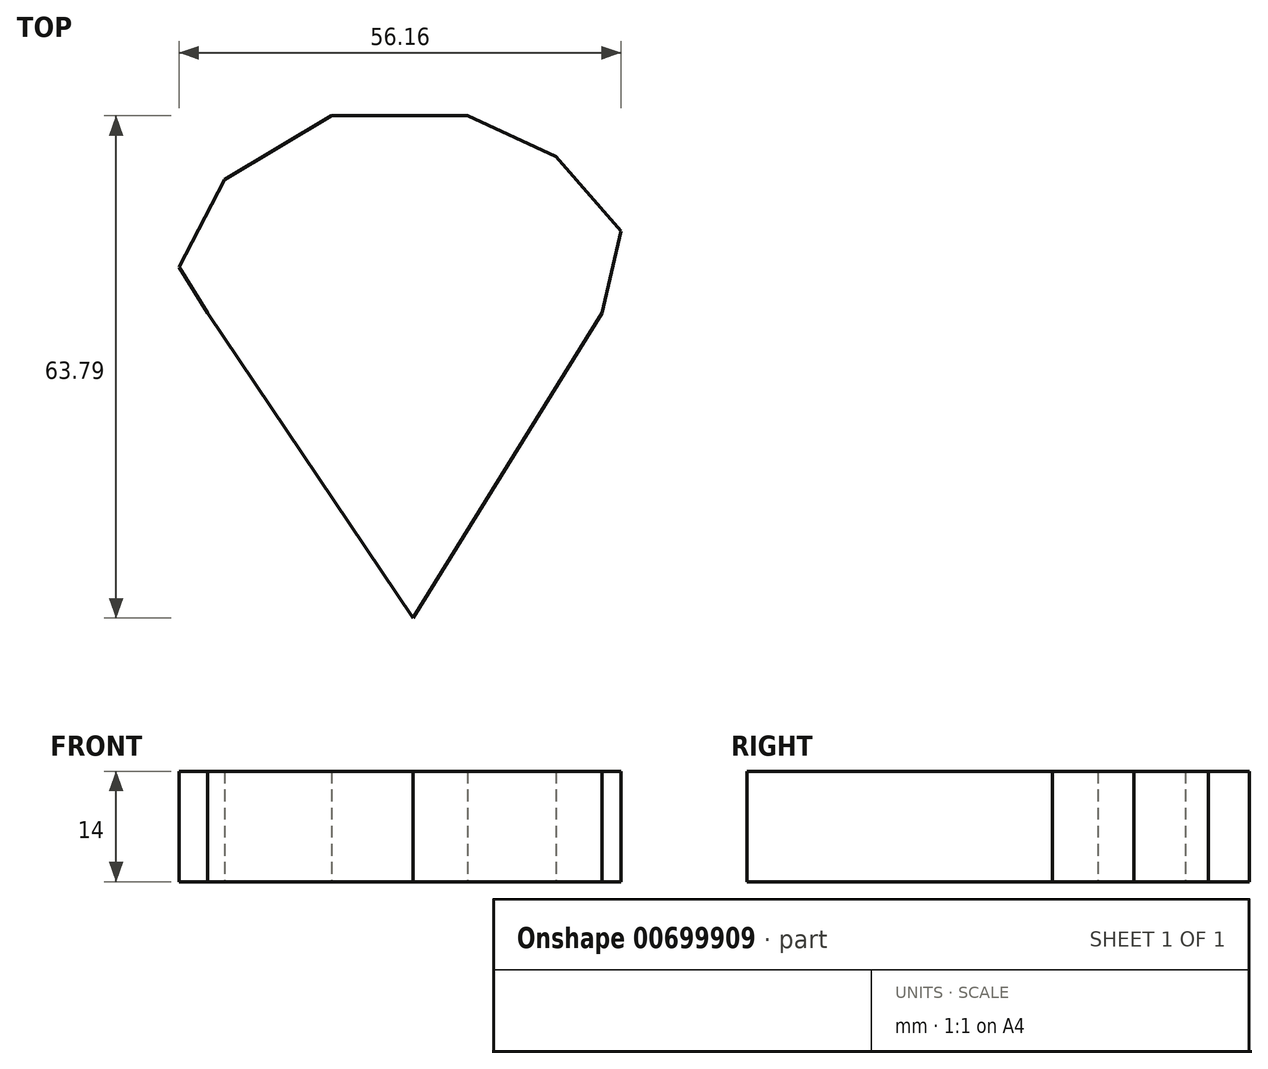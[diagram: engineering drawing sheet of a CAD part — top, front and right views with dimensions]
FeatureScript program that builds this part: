
annotation { "Feature Type Name" : "Feature", "Feature Type Description" : "" }
export const myFeature = defineFeature(function(context is Context, id is Id, definition is map)
    precondition{}
    {
        {
            var Q0;
            Q0=qCreatedBy(makeId("Top.planeOp"),FACE);
            var sketch = newSketch(context, id + "F0", { "sketchPlane" : qUnion([Q0])});
            skLineSegment(sketch, "E0.bottom", {"start": v(-39.53, 38.3) * mm, "end": v(60.28, 38.3) * mm});
            skLineSegment(sketch, "E0.top", {"start": v(-39.53, -55.7) * mm, "end": v(60.28, -55.7) * mm});
            skLineSegment(sketch, "E0.left", {"start": v(-39.53, 38.3) * mm, "end": v(-39.53, -55.7) * mm});
            skLineSegment(sketch, "E0.right", {"start": v(60.28, 38.3) * mm, "end": v(60.28, -55.7) * mm});
            skLineSegment(sketch, "E1", {"start": v(10.38, -55.7) * mm, "end": v(-15.72, -16.94) * mm});
            skLineSegment(sketch, "E2", {"start": v(10.38, -55.7) * mm, "end": v(34.34, -16.94) * mm});
            skLineSegment(sketch, "E3", {"start": v(-15.72, -16.94) * mm, "end": v(-19.38, -11.14) * mm});
            skLineSegment(sketch, "E4", {"start": v(-19.38, -11.14) * mm, "end": v(-13.58, 0) * mm});
            skLineSegment(sketch, "E5", {"start": v(-13.58, 0) * mm, "end": v(0, 8.09) * mm});
            skLineSegment(sketch, "E6", {"start": v(0, 8.09) * mm, "end": v(17.25, 8.09) * mm});
            skLineSegment(sketch, "E7", {"start": v(17.25, 8.09) * mm, "end": v(28.54, 2.9) * mm});
            skLineSegment(sketch, "E8", {"start": v(28.54, 2.9) * mm, "end": v(36.78, -6.56) * mm});
            skLineSegment(sketch, "E9", {"start": v(36.78, -6.56) * mm, "end": v(34.34, -16.94) * mm});
            skSolve(sketch);
        }
        {
            var Q0;
            Q0=makeQuery(id+"F0.imprint","IMPRINT",FACE,{"disambiguationData":[TD([[makeQuery(id+"F0.imprint","IMPRINT",EDGE,{"derivedFrom":sQuery(id+"F0.wireOp",EDGE,"E1")}),-1.0]])]});
            extrude(context, id + "F1", {"entities" : qUnion([Q0]), "depth" : 14 * mm, "offsetDistance" : 25 * mm});
        }
    });
